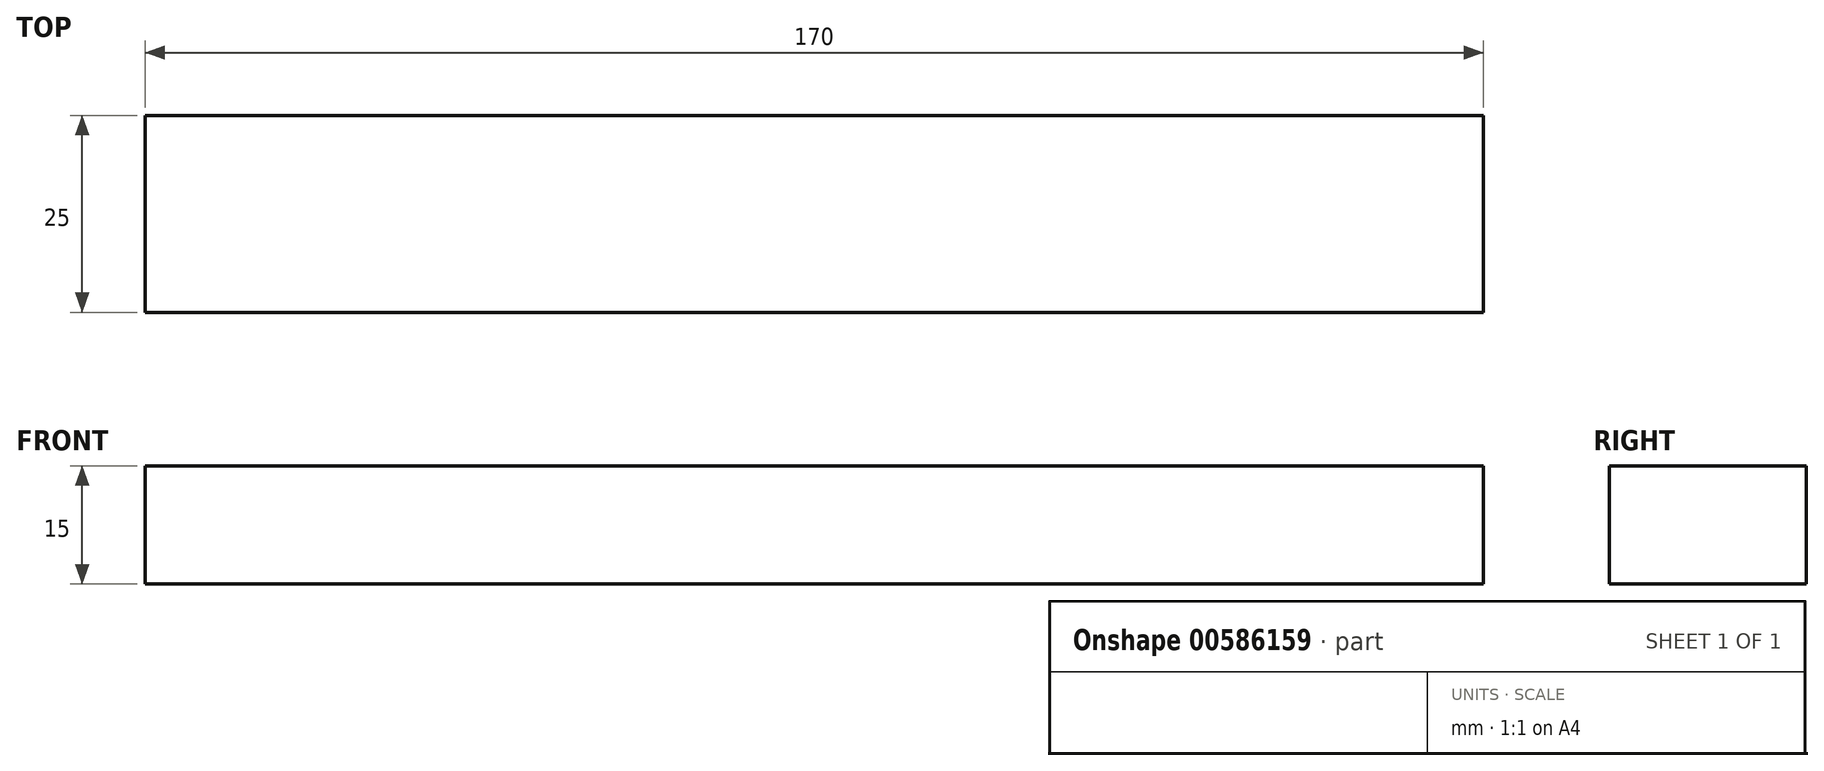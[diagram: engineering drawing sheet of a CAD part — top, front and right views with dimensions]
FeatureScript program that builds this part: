
annotation { "Feature Type Name" : "Feature", "Feature Type Description" : "" }
export const myFeature = defineFeature(function(context is Context, id is Id, definition is map)
    precondition{}
    {
        {
            var Q0;
            Q0=qCreatedBy(makeId("Top.planeOp"),FACE);
            var sketch = newSketch(context, id + "F0", { "sketchPlane" : qUnion([Q0])});
            skLineSegment(sketch, "E0.bottom", {"start": v(85, -12.5) * mm, "end": v(-85, -12.5) * mm});
            skLineSegment(sketch, "E0.top", {"start": v(85, 12.5) * mm, "end": v(-85, 12.5) * mm});
            skLineSegment(sketch, "E0.left", {"start": v(85, -12.5) * mm, "end": v(85, 12.5) * mm});
            skLineSegment(sketch, "E0.right", {"start": v(-85, -12.5) * mm, "end": v(-85, 12.5) * mm});
            skPoint(sketch, "E0.middle", {"position": v(0, 0) * mm});
            skSolve(sketch);
        }
        {
            var Q0;
            Q0 = qSketchRegion(id + "F0", true);
            extrude(context, id + "F1", {"entities" : qUnion([Q0]), "depth" : 15 * mm, "offsetDistance" : 25.4 * mm});
        }
    });
